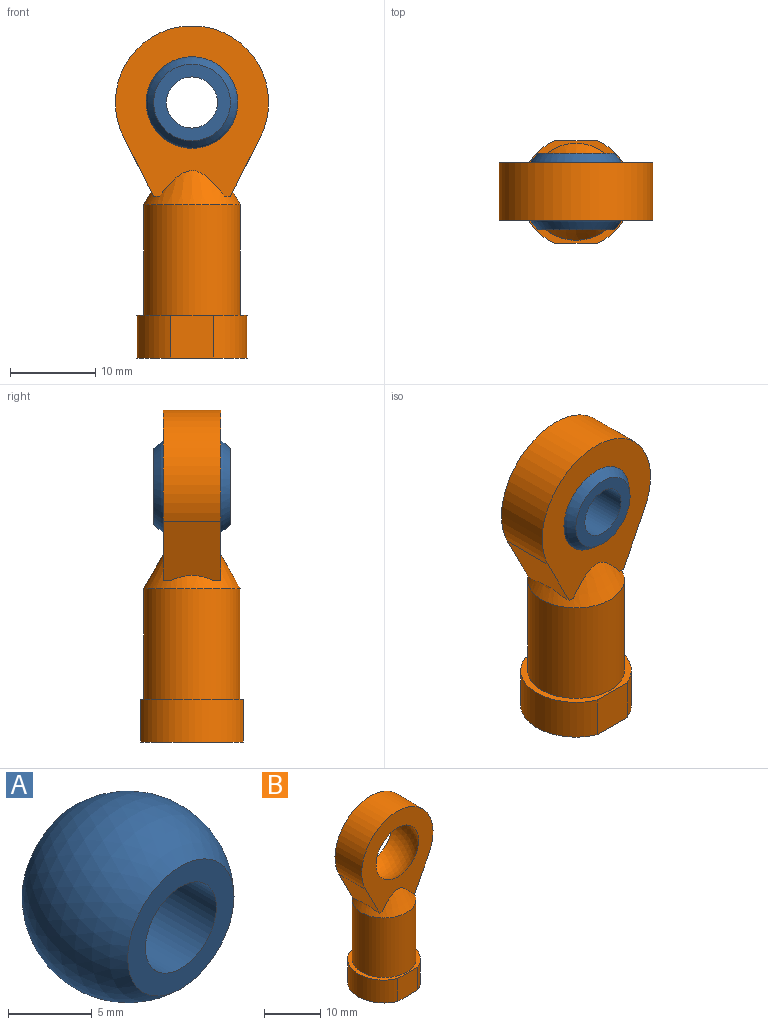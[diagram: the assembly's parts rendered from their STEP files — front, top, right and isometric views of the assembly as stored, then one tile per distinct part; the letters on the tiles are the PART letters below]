
ASSEMBLY  parts=2 mates=1
PART A: 4 faces, bbox 12.7x9x12.7 mm
  f0: plane 9x9mm, normal (0,-1,0), area 35.3mm2, adj f1,f3
  f1: sphere r=6.35mm, area 357.5mm2, adj f0,f2
  f2: plane 9x9mm, normal (0,1,0), area 35.3mm2, adj f1,f3
  f3: cylinder r=3mm len=8.96mm, axis (0,-1,0), area 168.9mm2, adj f0,f2
PART B: 20 faces, bbox 18x12x39 mm
  f0: plane 13x12mm, normal (0,0,-1), area 101.1mm2, adj f1,f13,f14,f18,f19
  f1: cylinder r=6.5mm len=12mm, axis (0,0,-1), area 76.4mm2, adj f0,f15,f18,f19
  f2: plane 6.92x6.75mm, normal (0.89,0,-0.45), area 50.4mm2, adj f4,f7,f8,f9,f10,f17
  f3: plane 6.92x6.75mm, normal (-0.89,0,-0.45), area 50.4mm2, adj f5,f6,f7,f8,f9,f17
  f4: plane 0.96x0.67mm, normal (0,0,-1), area 0.3mm2, adj f2,f7,f17
  f5: plane 0.96x0.67mm, normal (0,0,-1), area 0.3mm2, adj f3,f7,f17
  f6: plane 0.96x0.67mm, normal (0,0,-1), area 0.3mm2, adj f3,f8,f17
  f7: plane 20x18mm, normal (0,-1,0), area 179.2mm2, adj f2,f3,f4,f5,f9,f11,f17
  f8: plane 20x18mm, normal (0,1,0), area 179.1mm2, adj f2,f3,f6,f9,f10,f11,f17
  f9: cylinder r=9mm len=18mm, axis (0,1,0), area 248.1mm2, adj f2,f3,f7,f8
  f10: plane 0.96x0.67mm, normal (0,0,-1), area 0.3mm2, adj f2,f8,f17
  f11: sphere r=6.35mm, area 269.3mm2, adj f7,f8
  f12: cone r=3mm half-angle=60deg, axis (0,0,-1), area 32.6mm2, adj f13
  f13: cylinder r=3mm len=14.27mm, axis (0,0,-1), area 268.9mm2, adj f0,f12
  f14: cylinder r=6.5mm len=12mm, axis (0,0,-1), area 76.4mm2, adj f0,f15,f18,f19
  f15: plane 13x12mm, normal (0,0,1), area 27.9mm2, adj f1,f14,f16,f18,f19
  f16: cylinder r=5.68mm len=13mm, axis (0,0,-1), area 464.3mm2, adj f15,f17
  f17: cone r=3.38mm half-angle=30deg, axis (0,0,-1), area 80.2mm2, adj f2,f3,f4,f5,f6,f7,f8,f10
  f18: plane 5x5mm, normal (0,-1,0), area 25mm2, adj f0,f1,f14,f15
  f19: plane 5x5mm, normal (0,1,0), area 25mm2, adj f0,f1,f14,f15
PLACE A t=(-13.5,-7.46,0.5)mm
PLACE B t=(-13.5,-7.46,0.5)mm
MATE ball B.f1 <-> A.f1  axis (0,0,1) through (-13.5,-7.46,0.5)mm
